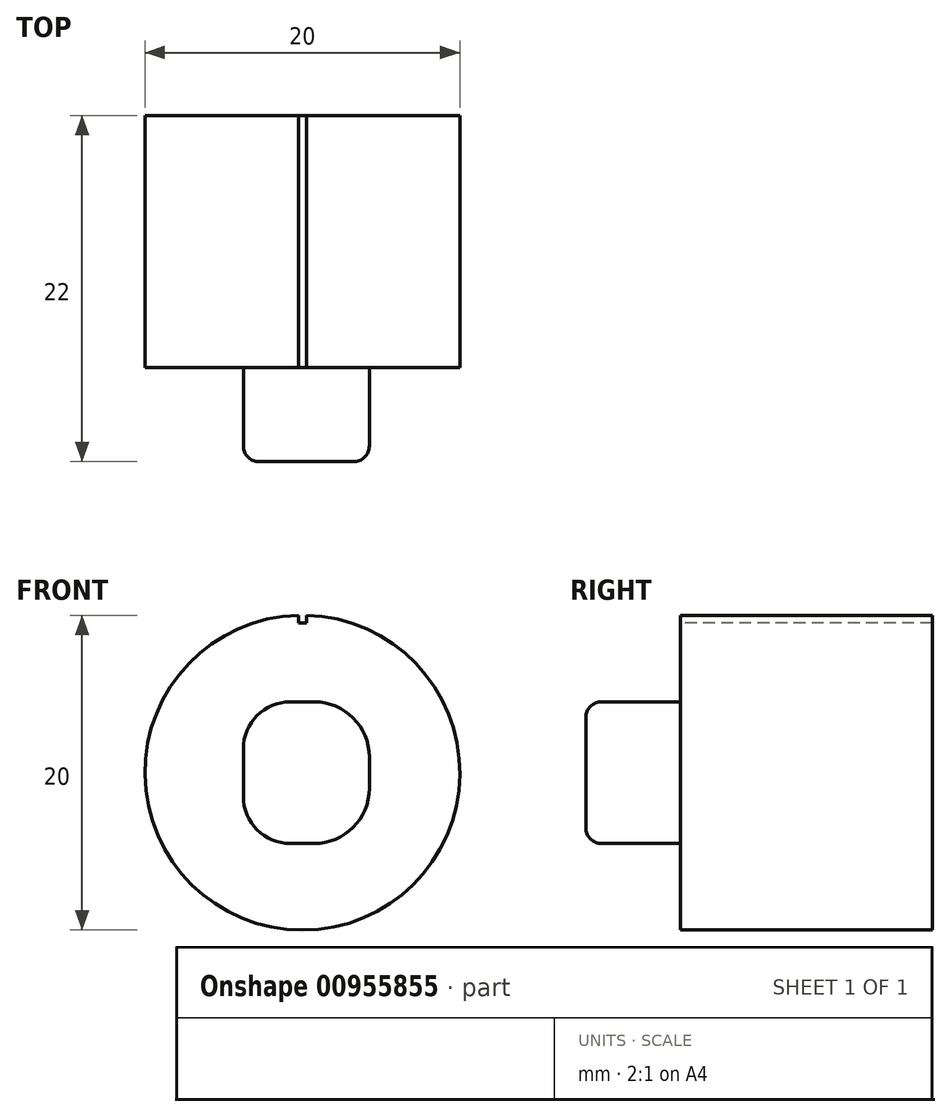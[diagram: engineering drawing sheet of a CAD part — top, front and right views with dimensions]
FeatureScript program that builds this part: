
annotation { "Feature Type Name" : "Feature", "Feature Type Description" : "" }
export const myFeature = defineFeature(function(context is Context, id is Id, definition is map)
    precondition{}
    {
        {
            var Q0;
            Q0=qCreatedBy(makeId("Front.planeOp"),FACE);
            var sketch = newSketch(context, id + "F0", { "sketchPlane" : qUnion([Q0])});
            skLineSegment(sketch, "E0.bottom", {"start": v(-0.5, 7.6) * mm, "end": v(1, 7.6) * mm});
            skLineSegment(sketch, "E0.top", {"start": v(-0.5, -1.4) * mm, "end": v(1, -1.4) * mm});
            skLineSegment(sketch, "E0.left", {"start": v(-3.5, 4.6) * mm, "end": v(-3.5, 1.6) * mm});
            skLineSegment(sketch, "E0.right", {"start": v(4.5, 4.1) * mm, "end": v(4.5, 2.1) * mm});
            skPoint(sketch, "E1.visualSharp", {"position": v(4.5, 7.6) * mm});
            skArc(sketch, "E1.filletArc", {"start": v(4.5, 4.1) * mm, "mid": v(3.47, 6.58) * mm, "end": v(1, 7.6) * mm});
            skPoint(sketch, "E2.visualSharp", {"position": v(4.5, -1.4) * mm});
            skArc(sketch, "E2.filletArc", {"start": v(1, -1.4) * mm, "mid": v(3.47, -0.37) * mm, "end": v(4.5, 2.1) * mm});
            skPoint(sketch, "E3.visualSharp", {"position": v(-3.5, -1.4) * mm});
            skArc(sketch, "E3.filletArc", {"start": v(-3.5, 1.6) * mm, "mid": v(-2.62, -0.52) * mm, "end": v(-0.5, -1.4) * mm});
            skPoint(sketch, "E4.visualSharp", {"position": v(-3.5, 7.6) * mm});
            skArc(sketch, "E4.filletArc", {"start": v(-0.5, 7.6) * mm, "mid": v(-2.62, 6.72) * mm, "end": v(-3.5, 4.6) * mm});
            skSolve(sketch);
        }
        {
            var Q0;
            Q0=makeQuery(id+"F0.imprint","IMPRINT",FACE,{"disambiguationData":[TD([[makeQuery(id+"F0.imprint","IMPRINT",EDGE,{"derivedFrom":sQuery(id+"F0.wireOp",EDGE,"E0.bottom")}),-1.0]])]});
            extrude(context, id + "F1", {"entities" : qUnion([Q0]), "depth" : 6 * mm, "offsetDistance" : 25 * mm});
        }
        {
            var Q0;
            Q0=makeQuery(id+"F1.opExtrude","CAP_FACE",FACE,{"disambiguationData":[OSD([sQuery(id+"F0.wireOp",EDGE,"E0.bottom"),sQuery(id+"F0.wireOp",EDGE,"E0.top"),sQuery(id+"F0.wireOp",EDGE,"E0.left"),sQuery(id+"F0.wireOp",EDGE,"E0.right"),sQuery(id+"F0.wireOp",EDGE,"E1.filletArc"),sQuery(id+"F0.wireOp",EDGE,"E2.filletArc"),sQuery(id+"F0.wireOp",EDGE,"E3.filletArc"),sQuery(id+"F0.wireOp",EDGE,"E4.filletArc")])],"isStart":false});
            fillet(context, id + "F2", {"entities" : qUnion([Q0]), "radius" : 1 * mm, "tangentPropagation" : true, "allowEdgeOverflow" : false});
        }
        {
            var Q0;
            Q0=makeQuery(id+"F1.opExtrude","CAP_FACE",FACE,{"disambiguationData":[OSD([sQuery(id+"F0.wireOp",EDGE,"E0.bottom"),sQuery(id+"F0.wireOp",EDGE,"E0.top"),sQuery(id+"F0.wireOp",EDGE,"E0.left"),sQuery(id+"F0.wireOp",EDGE,"E0.right"),sQuery(id+"F0.wireOp",EDGE,"E1.filletArc"),sQuery(id+"F0.wireOp",EDGE,"E2.filletArc"),sQuery(id+"F0.wireOp",EDGE,"E3.filletArc"),sQuery(id+"F0.wireOp",EDGE,"E4.filletArc")])],"isStart":true});
            var sketch = newSketch(context, id + "F3", { "sketchPlane" : qUnion([Q0])});
            skLineSegment(sketch, "E5", {"start": v(3.5, 3.1) * mm, "end": v(-4.5, 3.1) * mm});
            skLineSegment(sketch, "E6", {"start": v(-0.25, 7.6) * mm, "end": v(-0.25, -1.4) * mm});
            skCircle(sketch, "E7", {"center": v(-0.25, 3.1) * mm, "radius": 10 * mm});
            skSolve(sketch);
        }
        {
            var Q0;
            Q0=makeQuery(id+"F3.imprint","IMPRINT",FACE,{"disambiguationData":[TD([[makeQuery(id+"F3.imprint","IMPRINT",EDGE,{"derivedFrom":sQuery(id+"F3.wireOp",EDGE,"E7")}),1.0]])]});
            var Q1;
            {var subQ0=makeQuery(id+"F1.opExtrude","CAP_EDGE",EDGE,{"disambiguationData":[OSD([sQuery(id+"F0.wireOp",EDGE,"E3.filletArc")])],"isStart":true});Q1=makeQuery(id+"F3.imprint","IMPRINT",FACE,{"disambiguationData":[TD([[makeQuery(id+"F3.imprint","IMPRINT",EDGE,{"derivedFrom":subQ0}),-1.0]])]});}
            var Q2;
            {var subQ0=makeQuery(id+"F1.opExtrude","CAP_EDGE",EDGE,{"disambiguationData":[OSD([sQuery(id+"F0.wireOp",EDGE,"E2.filletArc")])],"isStart":true});Q2=makeQuery(id+"F3.imprint","IMPRINT",FACE,{"disambiguationData":[TD([[makeQuery(id+"F3.imprint","IMPRINT",EDGE,{"derivedFrom":subQ0}),-1.0]])]});}
            var Q3;
            Q3=makeQuery(id+"F3.imprint","IMPRINT",FACE,{"disambiguationData":[TD([[makeQuery(id+"F3.imprint","IMPRINT",EDGE,{"derivedFrom":sQuery(id+"F3.wireOp",EDGE,"E7")}),1.0]])]});
            var Q4;
            {var subQ0=makeQuery(id+"F1.opExtrude","CAP_EDGE",EDGE,{"disambiguationData":[OSD([sQuery(id+"F0.wireOp",EDGE,"E4.filletArc")])],"isStart":true});Q4=makeQuery(id+"F3.imprint","IMPRINT",FACE,{"disambiguationData":[TD([[makeQuery(id+"F3.imprint","IMPRINT",EDGE,{"derivedFrom":subQ0}),-1.0]])]});}
            var Q5;
            {var subQ0=makeQuery(id+"F1.opExtrude","CAP_EDGE",EDGE,{"disambiguationData":[OSD([sQuery(id+"F0.wireOp",EDGE,"E1.filletArc")])],"isStart":true});Q5=makeQuery(id+"F3.imprint","IMPRINT",FACE,{"disambiguationData":[TD([[makeQuery(id+"F3.imprint","IMPRINT",EDGE,{"derivedFrom":subQ0}),-1.0]])]});}
            extrude(context, id + "F4", {"entities" : qUnion([Q0, Q1, Q2, Q3, Q4, Q5]), "operationType" : NewBodyOperationType.ADD, "depth" : 16 * mm, "offsetDistance" : 25 * mm});
        }
        {
            var Q0;
            Q0=makeQuery(id+"F4.opExtrude","CAP_FACE",FACE,{"disambiguationData":[OSD([sQuery(id+"F3.wireOp",EDGE,"E7")])],"isStart":true});
            var sketch = newSketch(context, id + "F5", { "sketchPlane" : qUnion([Q0])});
            skLineSegment(sketch, "E8", {"start": v(0.25, 7.6) * mm, "end": v(0.25, 14.48) * mm});
            skLineSegment(sketch, "E9.bottom", {"start": v(0, 13.1) * mm, "end": v(0.5, 13.1) * mm});
            skLineSegment(sketch, "E9.top", {"start": v(0, 12.6) * mm, "end": v(0.5, 12.6) * mm});
            skLineSegment(sketch, "E9.left", {"start": v(0, 13.1) * mm, "end": v(0, 12.6) * mm});
            skLineSegment(sketch, "E9.right", {"start": v(0.5, 13.1) * mm, "end": v(0.5, 12.6) * mm});
            skSolve(sketch);
        }
        {
            var Q0;
            {var subQ0=sQuery(id+"F5.wireOp",EDGE,"E9.top");var subQ5=sQuery(id+"F5.wireOp",EDGE,"E9.left");var subQ6=makeQuery(id+"F5.imprint","INTERSECT",VERTEX,{"derivedFrom":[subQ0,subQ5]});Q0=makeQuery(id+"F5.imprint","IMPRINT",FACE,{"disambiguationData":[TD([[makeQuery(id+"F5.imprint","IMPRINT",EDGE,{"disambiguationData":[TD([[subQ6,-1.0]])],"derivedFrom":subQ0}),1.0]])]});}
            var Q1;
            {var subQ0=sQuery(id+"F5.wireOp",EDGE,"E9.top");var subQ5=sQuery(id+"F5.wireOp",EDGE,"E9.right");var subQ7=makeQuery(id+"F5.imprint","INTERSECT",VERTEX,{"derivedFrom":[subQ0,subQ5]});Q1=makeQuery(id+"F5.imprint","IMPRINT",FACE,{"disambiguationData":[TD([[makeQuery(id+"F5.imprint","IMPRINT",EDGE,{"disambiguationData":[TD([[subQ7,1.0]])],"derivedFrom":subQ0}),1.0]])]});}
            extrude(context, id + "F6", {"entities" : qUnion([Q0, Q1]), "operationType" : NewBodyOperationType.REMOVE, "oppositeDirection" : true, "depth" : 25 * mm, "offsetDistance" : 25 * mm});
        }
    });
